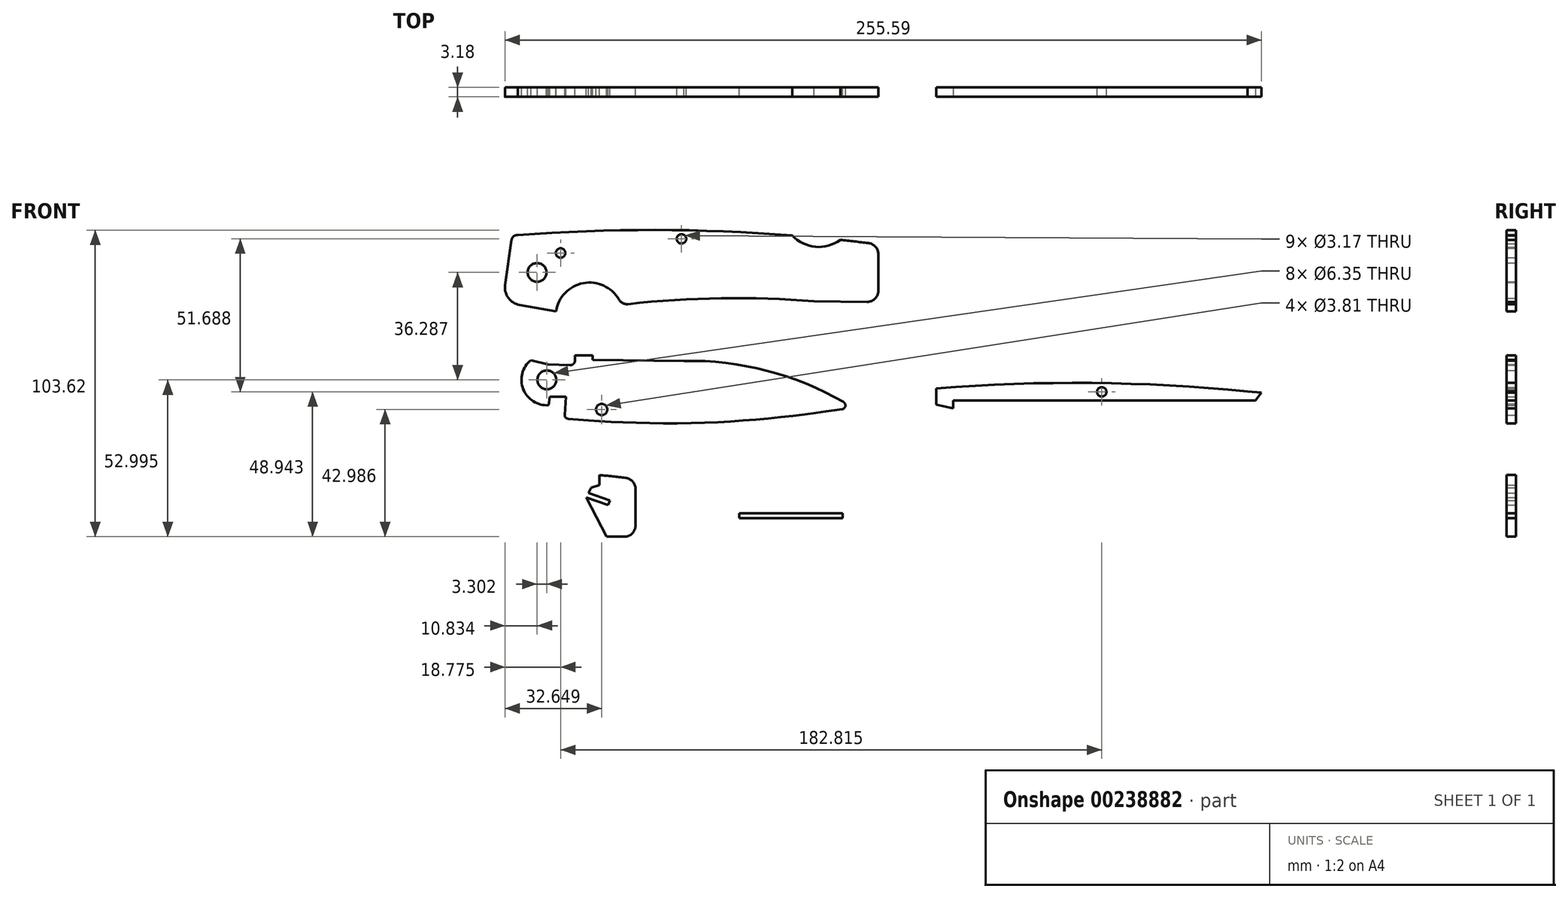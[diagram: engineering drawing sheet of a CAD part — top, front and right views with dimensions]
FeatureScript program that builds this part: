
annotation { "Feature Type Name" : "Feature", "Feature Type Description" : "" }
export const myFeature = defineFeature(function(context is Context, id is Id, definition is map)
    precondition{}
    {
        {
            var Q0;
            Q0=qCreatedBy(makeId("Front.planeOp"),FACE);
            var sketch = newSketch(context, id + "F0", { "sketchPlane" : qUnion([Q0])});
            skLineSegment(sketch, "E0", {"start": v(-111.57, 31.31) * mm, "end": v(-113.73, 16.08) * mm});
            skLineSegment(sketch, "E1", {"start": v(-96.53, 7.19) * mm, "end": v(-108.84, 9.35) * mm});
            skArc(sketch, "E2", {"start": v(-113.73, 16.08) * mm, "mid": v(-112.65, 11.72) * mm, "end": v(-108.84, 9.35) * mm});
            skPoint(sketch, "E2.first.point", {"position": v(-113.73, 16.08) * mm});
            skPoint(sketch, "E2.second.point", {"position": v(-112.97, 12.22) * mm});
            skPoint(sketch, "E2.third.point", {"position": v(-108.84, 9.35) * mm});
            skArc(sketch, "E3", {"start": v(-16.77, 32.83) * mm, "mid": v(-63.45, 34.67) * mm, "end": v(-110.13, 32.9) * mm});
            skPoint(sketch, "E3.first.point", {"position": v(-110.13, 32.9) * mm});
            skPoint(sketch, "E3.second.point", {"position": v(-61.22, 34.67) * mm});
            skPoint(sketch, "E3.third.point", {"position": v(-16.83, 32.83) * mm});
            skArc(sketch, "E4", {"start": v(-16.77, 32.83) * mm, "mid": v(-8.91, 29) * mm, "end": v(-0.5, 31.33) * mm});
            skPoint(sketch, "E4.first.point", {"position": v(-16.77, 32.83) * mm});
            skPoint(sketch, "E4.second.point", {"position": v(-7.82, 28.95) * mm});
            skPoint(sketch, "E4.third.point", {"position": v(-0.5, 31.33) * mm});
            skArc(sketch, "E5", {"start": v(-75.32, 11.2) * mm, "mid": v(-87.35, 16.73) * mm, "end": v(-96.53, 7.19) * mm});
            skArc(sketch, "E6", {"start": v(-9.33, 10.62) * mm, "mid": v(-40.8, 11.64) * mm, "end": v(-72.23, 9.64) * mm});
            skArc(sketch, "E7", {"start": v(-75.32, 11.2) * mm, "mid": v(-74.01, 9.96) * mm, "end": v(-72.23, 9.64) * mm});
            skPoint(sketch, "E7.first.point", {"position": v(-75.32, 11.2) * mm});
            skPoint(sketch, "E7.second.point", {"position": v(-73.68, 9.81) * mm});
            skPoint(sketch, "E7.third.point", {"position": v(-72.23, 9.64) * mm});
            skArc(sketch, "E8.trimOffspring", {"start": v(-75.32, 11.2) * mm, "mid": v(-80.66, 15.97) * mm, "end": v(-87.78, 16.64) * mm});
            skCircle(sketch, "E9", {"center": v(-102.96, 20.33) * mm, "radius": 3.18 * mm});
            skCircle(sketch, "E10", {"center": v(-95.01, 26.9) * mm, "radius": 1.59 * mm});
            skCircle(sketch, "E11", {"center": v(-54.16, 31.68) * mm, "radius": 1.59 * mm});
            skLineSegment(sketch, "E12", {"start": v(12.33, 26.47) * mm, "end": v(12.33, 14.2) * mm});
            skLineSegment(sketch, "E13", {"start": v(8.47, 10.39) * mm, "end": v(-9.33, 10.62) * mm});
            skArc(sketch, "E14", {"start": v(8.47, 10.39) * mm, "mid": v(11.2, 11.49) * mm, "end": v(12.33, 14.2) * mm});
            skArc(sketch, "E15.trimOffspring", {"start": v(8.98, 30.25) * mm, "mid": v(4.24, 30.81) * mm, "end": v(-0.5, 31.33) * mm});
            skArc(sketch, "E16", {"start": v(12.33, 26.47) * mm, "mid": v(11.37, 29) * mm, "end": v(8.98, 30.25) * mm});
            skPoint(sketch, "E17.orphan", {"position": v(12.33, 29.84) * mm});
            skLineSegment(sketch, "E18", {"start": v(31.9, -24.28) * mm, "end": v(31.9, -18.8) * mm});
            skLineSegment(sketch, "E19", {"start": v(31.9, -24.28) * mm, "end": v(37.6, -25.76) * mm});
            skLineSegment(sketch, "E20", {"start": v(37.6, -25.76) * mm, "end": v(37.6, -22.95) * mm});
            skLineSegment(sketch, "E21", {"start": v(37.6, -22.95) * mm, "end": v(137.02, -22.95) * mm});
            skLineSegment(sketch, "E22", {"start": v(137.02, -22.95) * mm, "end": v(139.23, -20.03) * mm});
            skArc(sketch, "E23", {"start": v(139.23, -20.03) * mm, "mid": v(85.6, -17.02) * mm, "end": v(31.9, -18.8) * mm});
            skLineSegment(sketch, "E24.bottom", {"start": v(-34.72, -61.08) * mm, "end": v(0.2, -61.08) * mm});
            skLineSegment(sketch, "E24.top", {"start": v(-34.72, -62.73) * mm, "end": v(0.2, -62.73) * mm});
            skLineSegment(sketch, "E24.left", {"start": v(-34.72, -61.08) * mm, "end": v(-34.72, -62.73) * mm});
            skLineSegment(sketch, "E24.right", {"start": v(0.2, -61.08) * mm, "end": v(0.2, -62.73) * mm});
            skLineSegment(sketch, "E25", {"start": v(-86.33, -55.63) * mm, "end": v(-79.54, -68.88) * mm});
            skLineSegment(sketch, "E26", {"start": v(-82.53, -48) * mm, "end": v(-85.53, -54.13) * mm});
            skLineSegment(sketch, "E27", {"start": v(-85.53, -54.13) * mm, "end": v(-78.39, -56.71) * mm});
            skLineSegment(sketch, "E28", {"start": v(-78.39, -56.71) * mm, "end": v(-78.96, -58.29) * mm});
            skLineSegment(sketch, "E29", {"start": v(-78.96, -58.29) * mm, "end": v(-86.33, -55.63) * mm});
            skLineSegment(sketch, "E30", {"start": v(-69.7, -52.87) * mm, "end": v(-69.7, -65.14) * mm});
            skLineSegment(sketch, "E31", {"start": v(-73.56, -68.95) * mm, "end": v(-79.54, -68.88) * mm});
            skArc(sketch, "E32", {"start": v(-73.56, -68.95) * mm, "mid": v(-70.84, -67.85) * mm, "end": v(-69.7, -65.14) * mm});
            skArc(sketch, "E33.trimOffspring", {"start": v(-73.05, -49.09) * mm, "mid": v(-77.79, -48.53) * mm, "end": v(-82.53, -48) * mm});
            skArc(sketch, "E34", {"start": v(-69.7, -52.87) * mm, "mid": v(-70.66, -50.34) * mm, "end": v(-73.05, -49.09) * mm});
            skPoint(sketch, "E35.orphan", {"position": v(-69.7, -49.5) * mm});
            skCircle(sketch, "E36", {"center": v(-99.65, -15.96) * mm, "radius": 3.18 * mm});
            skCircle(sketch, "E37", {"center": v(-81.14, -25.96) * mm, "radius": 1.9 * mm});
            skLineSegment(sketch, "E38", {"start": v(-90.15, -7.62) * mm, "end": v(-84.13, -7.62) * mm});
            skLineSegment(sketch, "E39", {"start": v(-84.13, -7.62) * mm, "end": v(-84.13, -9.15) * mm});
            skLineSegment(sketch, "E40", {"start": v(-105.04, -9.29) * mm, "end": v(-99.25, -10.7) * mm});
            skLineSegment(sketch, "E41", {"start": v(-99.25, -10.7) * mm, "end": v(-91.8, -10.98) * mm});
            skLineSegment(sketch, "E42", {"start": v(-90.15, -7.62) * mm, "end": v(-90.15, -9.4) * mm});
            skArc(sketch, "E43", {"start": v(-91.8, -10.98) * mm, "mid": v(-90.63, -10.54) * mm, "end": v(-90.15, -9.4) * mm});
            skArc(sketch, "E44", {"start": v(-105.04, -9.29) * mm, "mid": v(-107.63, -19.1) * mm, "end": v(-99.02, -24.5) * mm});
            skLineSegment(sketch, "E45", {"start": v(-99.02, -24.5) * mm, "end": v(-98.73, -21.6) * mm});
            skLineSegment(sketch, "E46", {"start": v(-98.73, -21.6) * mm, "end": v(-93.2, -21.6) * mm});
            skLineSegment(sketch, "E47", {"start": v(-93.2, -21.6) * mm, "end": v(-93.73, -29) * mm});
            skLineSegment(sketch, "E48", {"start": v(-84.13, -9.15) * mm, "end": v(-53.31, -9.53) * mm});
            skArc(sketch, "E49", {"start": v(3.64, -25.31) * mm, "mid": v(-23.7, -13.3) * mm, "end": v(-53.31, -9.53) * mm});
            skFitSpline(sketch, "E50", {"points": [v(-93.73, -29) * mm, v(-76.51, -30.18) * mm, v(-49.65, -30.52) * mm, v(-25.17, -29) * mm, v(-5.36, -26.65) * mm, v(3.64, -25.31) * mm], "startDerivative": vector(84.42, -6.94) * mm, "endDerivative": vector(58.31, 8.48) * mm});
            skArc(sketch, "E51.trimOffspring", {"start": v(3.64, -25.31) * mm, "mid": v(-8.22, -18.94) * mm, "end": v(-20.8, -14.15) * mm});
            skArc(sketch, "E52", {"start": v(-109.52, 32.95) * mm, "mid": v(-110.87, 32.54) * mm, "end": v(-111.57, 31.31) * mm});
            skCircle(sketch, "E53", {"center": v(87.8, -20) * mm, "radius": 1.59 * mm});
            skPoint(sketch, "E54", {"position": v(87.9, -19.96) * mm});
            skSolve(sketch);
        }
        {
            var Q0;
            Q0 = qSketchRegion(id + "F0", true);
            extrude(context, id + "F1", {"entities" : qUnion([Q0]), "depth" : 3.17 * mm});
        }
        {
            var Q0;
            Q0=makeQuery(id+"F1.opExtrude","CAP_FACE",FACE,{"disambiguationData":[OSD([sQuery(id+"F0.wireOp",EDGE,"E18"),sQuery(id+"F0.wireOp",EDGE,"E19"),sQuery(id+"F0.wireOp",EDGE,"E20"),sQuery(id+"F0.wireOp",EDGE,"E21"),sQuery(id+"F0.wireOp",EDGE,"E22"),sQuery(id+"F0.wireOp",EDGE,"E23"),sQuery(id+"F0.wireOp",EDGE,"E53")])],"isStart":false});
            var sketch = newSketch(context, id + "F2", { "sketchPlane" : qUnion([Q0])});
            skLineSegment(sketch, "E55", {"start": v(31.9, -24.28) * mm, "end": v(37.6, -25.63) * mm});
            skLineSegment(sketch, "E56", {"start": v(37.6, -25.63) * mm, "end": v(37.6, -25.76) * mm});
            skLineSegment(sketch, "E57", {"start": v(37.6, -25.76) * mm, "end": v(31.9, -24.28) * mm});
            skSolve(sketch);
        }
        {
            var Q0;
            Q0 = qSketchRegion(id + "F2", true);
            extrude(context, id + "F3", {"entities" : qUnion([Q0]), "operationType" : NewBodyOperationType.REMOVE, "oppositeDirection" : true, "depth" : 25.4 * mm});
        }
        {
            var Q0;
            Q0=makeQuery(id+"F1.opExtrude","CAP_FACE",FACE,{"disambiguationData":[OSD([sQuery(id+"F0.wireOp",EDGE,"E18"),sQuery(id+"F0.wireOp",EDGE,"E19"),sQuery(id+"F0.wireOp",EDGE,"E20"),sQuery(id+"F0.wireOp",EDGE,"E21"),sQuery(id+"F0.wireOp",EDGE,"E22"),sQuery(id+"F0.wireOp",EDGE,"E23"),sQuery(id+"F0.wireOp",EDGE,"E53")])],"isStart":false});
            var sketch = newSketch(context, id + "F4", { "sketchPlane" : qUnion([Q0])});
            skLineSegment(sketch, "E58", {"start": v(134.64, -22.95) * mm, "end": v(139.72, -22.95) * mm});
            skLineSegment(sketch, "E59", {"start": v(139.72, -22.95) * mm, "end": v(141.8, -20.21) * mm});
            skLineSegment(sketch, "E60", {"start": v(141.8, -20.21) * mm, "end": v(137.02, -19.81) * mm});
            skLineSegment(sketch, "E61", {"start": v(137.02, -19.81) * mm, "end": v(134.64, -22.95) * mm});
            skSolve(sketch);
        }
        {
            var Q0;
            Q0 = qSketchRegion(id + "F4", true);
            extrude(context, id + "F5", {"entities" : qUnion([Q0]), "operationType" : NewBodyOperationType.ADD, "oppositeDirection" : true, "depth" : 3.17 * mm});
        }
        {
            var Q0;
            Q0=makeQuery(id+"F1.opExtrude","CAP_FACE",FACE,{"disambiguationData":[OSD([sQuery(id+"F0.wireOp",EDGE,"E25"),sQuery(id+"F0.wireOp",EDGE,"E26"),sQuery(id+"F0.wireOp",EDGE,"E27"),sQuery(id+"F0.wireOp",EDGE,"E28"),sQuery(id+"F0.wireOp",EDGE,"E29"),sQuery(id+"F0.wireOp",EDGE,"E30"),sQuery(id+"F0.wireOp",EDGE,"E31"),sQuery(id+"F0.wireOp",EDGE,"E32"),sQuery(id+"F0.wireOp",EDGE,"E33.trimOffspring"),sQuery(id+"F0.wireOp",EDGE,"E34")])],"isStart":true});
            var sketch = newSketch(context, id + "F6", { "sketchPlane" : qUnion([Q0])});
            skLineSegment(sketch, "E62", {"start": v(81.85, -48.08) * mm, "end": v(81.85, -51.44) * mm});
            skLineSegment(sketch, "E63", {"start": v(81.85, -51.44) * mm, "end": v(84.69, -52.41) * mm});
            skLineSegment(sketch, "E64", {"start": v(84.69, -52.41) * mm, "end": v(82.53, -48) * mm});
            skLineSegment(sketch, "E65", {"start": v(82.53, -48) * mm, "end": v(81.85, -48.08) * mm});
            skSolve(sketch);
        }
        {
            var Q0;
            Q0 = qSketchRegion(id + "F6", true);
            extrude(context, id + "F7", {"entities" : qUnion([Q0]), "operationType" : NewBodyOperationType.REMOVE, "oppositeDirection" : true, "depth" : 25.4 * mm});
        }
        {
            var Q0;
            Q0=makeQuery(id+"F1.opExtrude","SWEPT_EDGE",EDGE,{"disambiguationData":[OSD([sQuery(id+"F0.wireOp",EDGE,"E50"),sQuery(id+"F0.wireOp",EDGE,"E51.trimOffspring")])]});
            fillet(context, id + "F8", {"entities" : qUnion([Q0]), "radius" : 1.27 * mm, "tangentPropagation" : true, "allowEdgeOverflow" : false});
        }
    });
